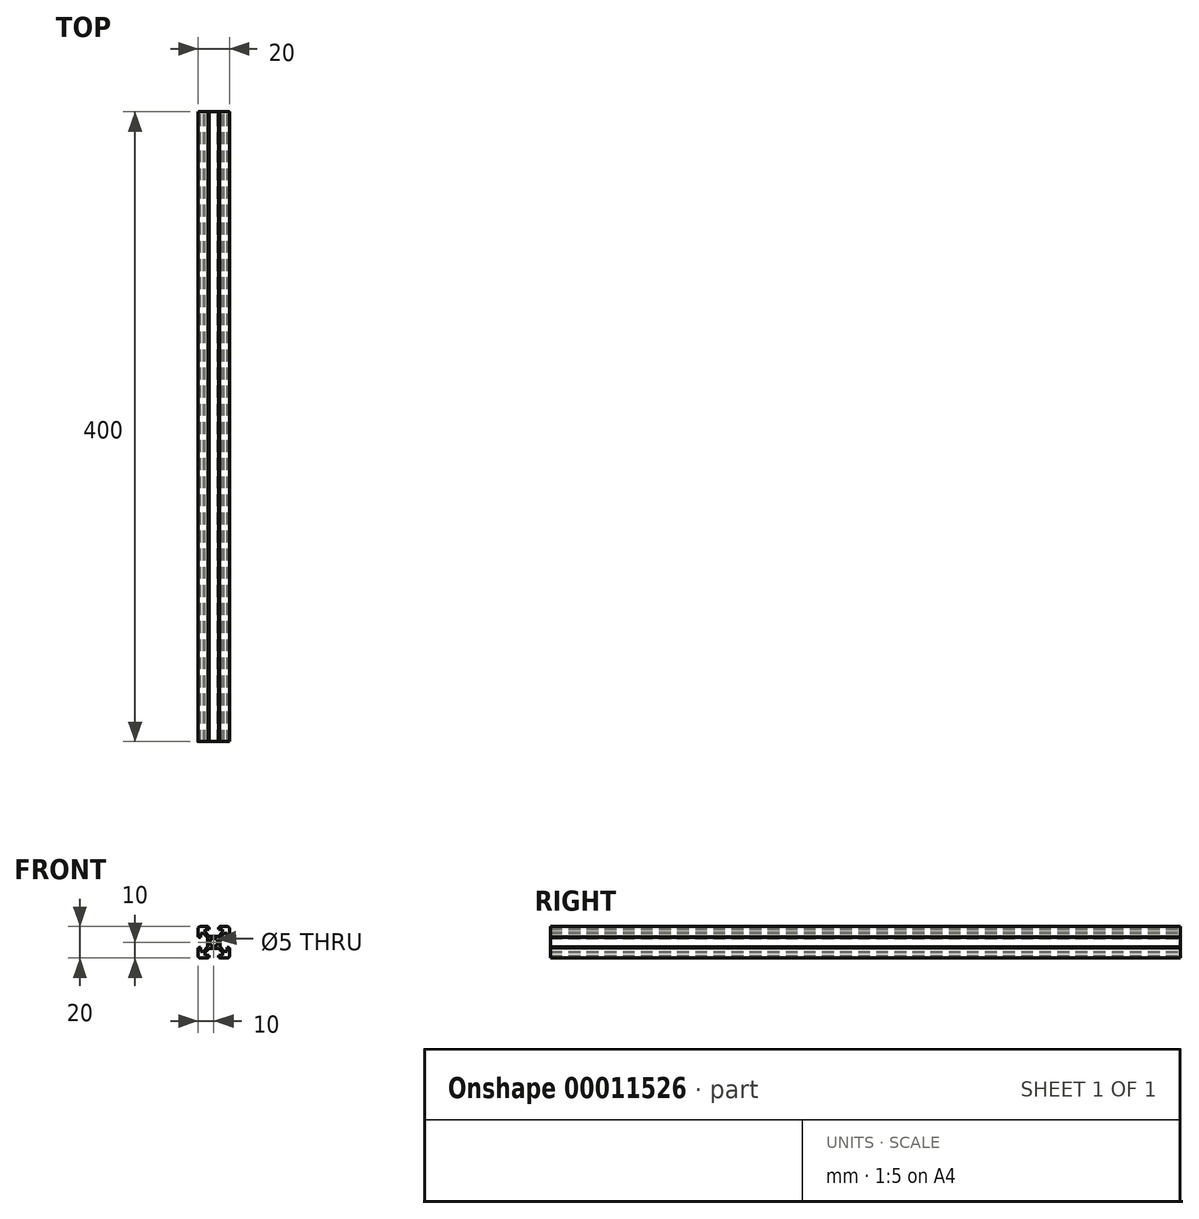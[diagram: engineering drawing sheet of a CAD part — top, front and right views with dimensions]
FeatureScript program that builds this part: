
annotation { "Feature Type Name" : "Feature", "Feature Type Description" : "" }
export const myFeature = defineFeature(function(context is Context, id is Id, definition is map)
    precondition{}
    {
        {
            var Q0;
            Q0=qCreatedBy(makeId("Front.planeOp"),FACE);
            var sketch = newSketch(context, id + "F0", { "sketchPlane" : qUnion([Q0])});
            skLineSegment(sketch, "E0", {"start": v(-10, 8.5) * mm, "end": v(-10, 3.6) * mm});
            skLineSegment(sketch, "E1", {"start": v(-10, 3.6) * mm, "end": v(-9.5, 3.6) * mm});
            skLineSegment(sketch, "E2", {"start": v(-9.5, 3.6) * mm, "end": v(-9.5, 3.1) * mm});
            skLineSegment(sketch, "E3", {"start": v(-9.5, 3.1) * mm, "end": v(-8.3, 3.1) * mm});
            skLineSegment(sketch, "E4", {"start": v(-8.3, 3.1) * mm, "end": v(-8.3, 5.63) * mm});
            skLineSegment(sketch, "E5", {"start": v(-8.3, 5.63) * mm, "end": v(-6.53, 5.63) * mm});
            skLineSegment(sketch, "E6", {"start": v(-6.53, 5.63) * mm, "end": v(-3.9, 3) * mm});
            skLineSegment(sketch, "E7", {"start": v(-8.5, 10) * mm, "end": v(-3.6, 10) * mm});
            skLineSegment(sketch, "E8", {"start": v(-3.6, 10) * mm, "end": v(-3.6, 9.5) * mm});
            skLineSegment(sketch, "E9", {"start": v(-3.6, 9.5) * mm, "end": v(-3.1, 9.5) * mm});
            skLineSegment(sketch, "E10", {"start": v(-3.1, 9.5) * mm, "end": v(-3.1, 8.3) * mm});
            skLineSegment(sketch, "E11", {"start": v(-3.1, 8.3) * mm, "end": v(-5.63, 8.3) * mm});
            skLineSegment(sketch, "E12", {"start": v(-5.63, 8.3) * mm, "end": v(-5.63, 6.53) * mm});
            skLineSegment(sketch, "E13", {"start": v(-5.63, 6.53) * mm, "end": v(-3, 3.9) * mm});
            skPoint(sketch, "E14.visualSharp", {"position": v(-10, 10) * mm});
            skArc(sketch, "E14.filletArc", {"start": v(-8.5, 10) * mm, "mid": v(-9.56, 9.56) * mm, "end": v(-10, 8.5) * mm});
            skLineSegment(sketch, "E15.0.MirrorCS", {"start": v(3.1, 9.5) * mm, "end": v(3.1, 8.3) * mm});
            skLineSegment(sketch, "E15.1.MirrorCS", {"start": v(3.6, 9.5) * mm, "end": v(3.1, 9.5) * mm});
            skLineSegment(sketch, "E15.2.MirrorCS", {"start": v(3.6, 10) * mm, "end": v(3.6, 9.5) * mm});
            skLineSegment(sketch, "E15.3.MirrorCS", {"start": v(3.1, 8.3) * mm, "end": v(5.63, 8.3) * mm});
            skLineSegment(sketch, "E15.4.MirrorCS", {"start": v(9.5, 3.6) * mm, "end": v(9.5, 3.1) * mm});
            skLineSegment(sketch, "E15.5.MirrorCS", {"start": v(10, 3.6) * mm, "end": v(9.5, 3.6) * mm});
            skLineSegment(sketch, "E15.6.MirrorCS", {"start": v(8.3, 3.1) * mm, "end": v(8.3, 5.63) * mm});
            skArc(sketch, "E15.7.MirrorCS", {"start": v(8.5, 10) * mm, "mid": v(9.56, 9.56) * mm, "end": v(10, 8.5) * mm});
            skLineSegment(sketch, "E15.8.MirrorCS", {"start": v(9.5, 3.1) * mm, "end": v(8.3, 3.1) * mm});
            skLineSegment(sketch, "E15.9.MirrorCS", {"start": v(5.63, 8.3) * mm, "end": v(5.63, 6.53) * mm});
            skLineSegment(sketch, "E15.10.MirrorCS", {"start": v(8.3, 5.63) * mm, "end": v(6.53, 5.63) * mm});
            skLineSegment(sketch, "E15.12.MirrorCS", {"start": v(8.5, 10) * mm, "end": v(3.6, 10) * mm});
            skLineSegment(sketch, "E15.13.MirrorCS", {"start": v(6.53, 5.63) * mm, "end": v(3.9, 3) * mm});
            skPoint(sketch, "E15.14.MirrorP", {"position": v(10, 10) * mm});
            skLineSegment(sketch, "E15.15.MirrorCS", {"start": v(10, 8.5) * mm, "end": v(10, 3.6) * mm});
            skLineSegment(sketch, "E15.17.MirrorCS", {"start": v(5.63, 6.53) * mm, "end": v(3, 3.9) * mm});
            skLineSegment(sketch, "E16.0.MirrorCS", {"start": v(-5.63, -8.3) * mm, "end": v(-5.63, -6.53) * mm});
            skLineSegment(sketch, "E16.1.MirrorCS", {"start": v(-3.1, -9.5) * mm, "end": v(-3.1, -8.3) * mm});
            skLineSegment(sketch, "E16.2.MirrorCS", {"start": v(-3.1, -8.3) * mm, "end": v(-5.63, -8.3) * mm});
            skLineSegment(sketch, "E16.3.MirrorCS", {"start": v(-10, -3.6) * mm, "end": v(-9.5, -3.6) * mm});
            skLineSegment(sketch, "E16.4.MirrorCS", {"start": v(-3.6, -10) * mm, "end": v(-3.6, -9.5) * mm});
            skLineSegment(sketch, "E16.5.MirrorCS", {"start": v(8.3, -3.1) * mm, "end": v(8.3, -5.63) * mm});
            skLineSegment(sketch, "E16.6.MirrorCS", {"start": v(8.3, -5.63) * mm, "end": v(6.53, -5.63) * mm});
            skLineSegment(sketch, "E16.7.MirrorCS", {"start": v(3.1, -9.5) * mm, "end": v(3.1, -8.3) * mm});
            skLineSegment(sketch, "E16.8.MirrorCS", {"start": v(10, -3.6) * mm, "end": v(9.5, -3.6) * mm});
            skLineSegment(sketch, "E16.9.MirrorCS", {"start": v(9.5, -3.1) * mm, "end": v(8.3, -3.1) * mm});
            skLineSegment(sketch, "E16.10.MirrorCS", {"start": v(-10, -8.5) * mm, "end": v(-10, -3.6) * mm});
            skLineSegment(sketch, "E16.11.MirrorCS", {"start": v(-5.63, -6.53) * mm, "end": v(-3, -3.9) * mm});
            skLineSegment(sketch, "E16.12.MirrorCS", {"start": v(3.1, -8.3) * mm, "end": v(5.63, -8.3) * mm});
            skLineSegment(sketch, "E16.14.MirrorCS", {"start": v(10, -8.5) * mm, "end": v(10, -3.6) * mm});
            skLineSegment(sketch, "E16.15.MirrorCS", {"start": v(3.6, -10) * mm, "end": v(3.6, -9.5) * mm});
            skLineSegment(sketch, "E16.17.MirrorCS", {"start": v(8.5, -10) * mm, "end": v(3.6, -10) * mm});
            skLineSegment(sketch, "E16.18.MirrorCS", {"start": v(5.63, -8.3) * mm, "end": v(5.63, -6.53) * mm});
            skArc(sketch, "E16.20.MirrorCS", {"start": v(-8.5, -10) * mm, "mid": v(-9.56, -9.56) * mm, "end": v(-10, -8.5) * mm});
            skLineSegment(sketch, "E16.21.MirrorCS", {"start": v(6.53, -5.63) * mm, "end": v(3.9, -3) * mm});
            skLineSegment(sketch, "E16.22.MirrorCS", {"start": v(5.63, -6.53) * mm, "end": v(3, -3.9) * mm});
            skLineSegment(sketch, "E16.23.MirrorCS", {"start": v(-6.53, -5.63) * mm, "end": v(-3.9, -3) * mm});
            skLineSegment(sketch, "E16.25.MirrorCS", {"start": v(-8.5, -10) * mm, "end": v(-3.6, -10) * mm});
            skLineSegment(sketch, "E16.26.MirrorCS", {"start": v(-8.3, -5.63) * mm, "end": v(-6.53, -5.63) * mm});
            skLineSegment(sketch, "E16.27.MirrorCS", {"start": v(-8.3, -3.1) * mm, "end": v(-8.3, -5.63) * mm});
            skLineSegment(sketch, "E16.28.MirrorCS", {"start": v(-9.5, -3.1) * mm, "end": v(-8.3, -3.1) * mm});
            skArc(sketch, "E16.29.MirrorCS", {"start": v(8.5, -10) * mm, "mid": v(9.56, -9.56) * mm, "end": v(10, -8.5) * mm});
            skPoint(sketch, "E16.30.MirrorP", {"position": v(10, -10) * mm});
            skPoint(sketch, "E16.31.MirrorP", {"position": v(-10, -10) * mm});
            skCircle(sketch, "E17", {"center": v(0, 0) * mm, "radius": 2.5 * mm});
            skLineSegment(sketch, "E18", {"start": v(-9.5, -3.6) * mm, "end": v(-9.5, -3.1) * mm});
            skLineSegment(sketch, "E19", {"start": v(-3.1, -9.5) * mm, "end": v(-3.6, -9.5) * mm});
            skLineSegment(sketch, "E20", {"start": v(3.1, -9.5) * mm, "end": v(3.6, -9.5) * mm});
            skLineSegment(sketch, "E21", {"start": v(9.5, -3.6) * mm, "end": v(9.5, -3.1) * mm});
            skLineSegment(sketch, "E22", {"start": v(-3, 3.9) * mm, "end": v(3, 3.9) * mm});
            skLineSegment(sketch, "E23", {"start": v(3.9, 3) * mm, "end": v(3.9, -3) * mm});
            skLineSegment(sketch, "E24", {"start": v(3, -3.9) * mm, "end": v(-3, -3.9) * mm});
            skLineSegment(sketch, "E25", {"start": v(-3.9, -3) * mm, "end": v(-3.9, 3) * mm});
            skSolve(sketch);
        }
        {
            var Q0;
            Q0=makeQuery(id+"F0.imprint","IMPRINT",FACE,{"disambiguationData":[TD([[makeQuery(id+"F0.imprint","IMPRINT",EDGE,{"derivedFrom":sQuery(id+"F0.wireOp",EDGE,"E0")}),1.0]])]});
            extrude(context, id + "F1", {"entities" : qUnion([Q0]), "endBound" : BoundingType.SYMMETRIC, "depth" : 400 * mm});
        }
    });
